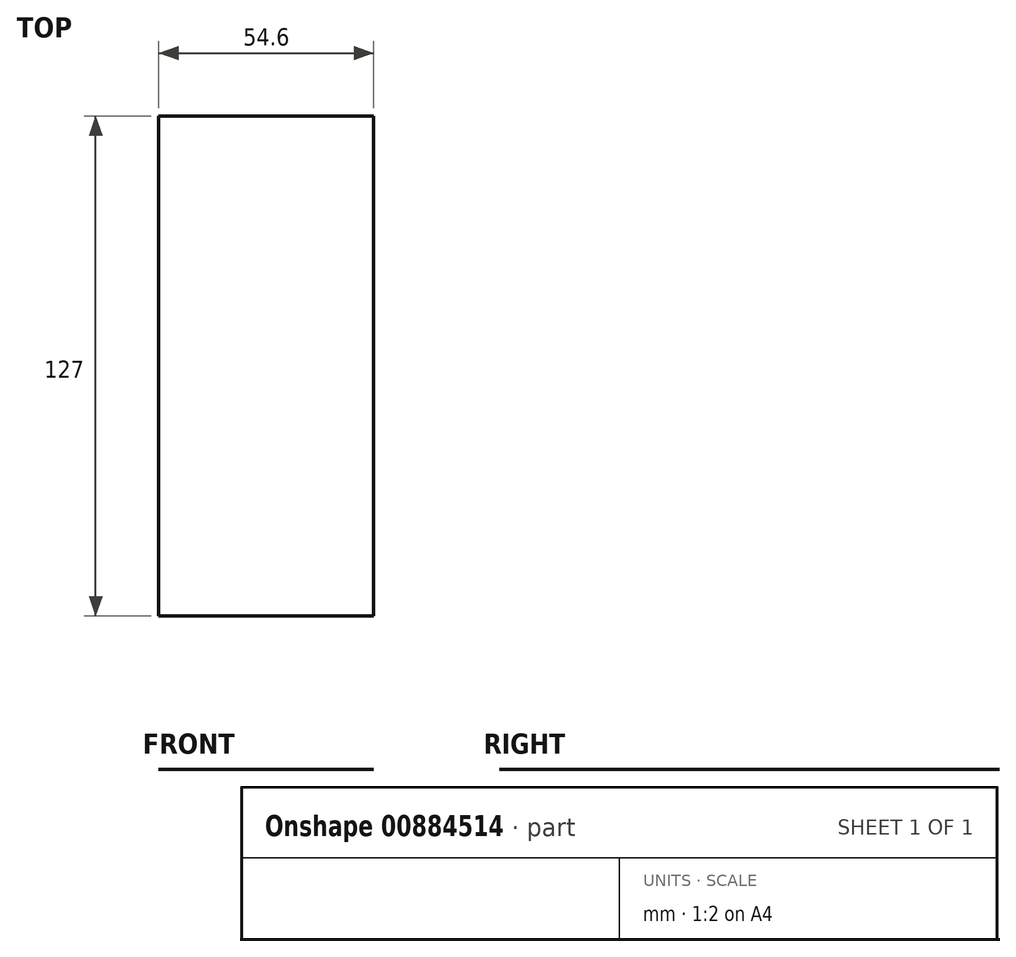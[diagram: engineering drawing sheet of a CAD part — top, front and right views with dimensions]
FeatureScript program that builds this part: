
annotation { "Feature Type Name" : "Feature", "Feature Type Description" : "" }
export const myFeature = defineFeature(function(context is Context, id is Id, definition is map)
    precondition{}
    {
        {
            var Q0;
            Q0=qCreatedBy(makeId("Front.planeOp"),FACE);
            var sketch = newSketch(context, id + "F0", { "sketchPlane" : qUnion([Q0])});
            skLineSegment(sketch, "E0.bottom", {"start": v(-20.95, 29.3) * mm, "end": v(33.65, 29.3) * mm});
            skLineSegment(sketch, "E0.top", {"start": v(-20.95, -37.45) * mm, "end": v(33.65, -37.45) * mm});
            skLineSegment(sketch, "E0.left", {"start": v(-20.95, 29.3) * mm, "end": v(-20.95, -37.45) * mm});
            skLineSegment(sketch, "E0.right", {"start": v(33.65, 29.3) * mm, "end": v(33.65, -37.45) * mm});
            skSolve(sketch);
        }
        {
            var Q0;
            Q0=sQuery(id+"F0.wireOp",EDGE,"E0.top");
            extrude(context, id + "F1", {"bodyType" : ToolBodyType.SURFACE, "surfaceEntities" : qUnion([Q0]), "depth" : 127 * mm, "offsetDistance" : 25.4 * mm});
        }
    });
